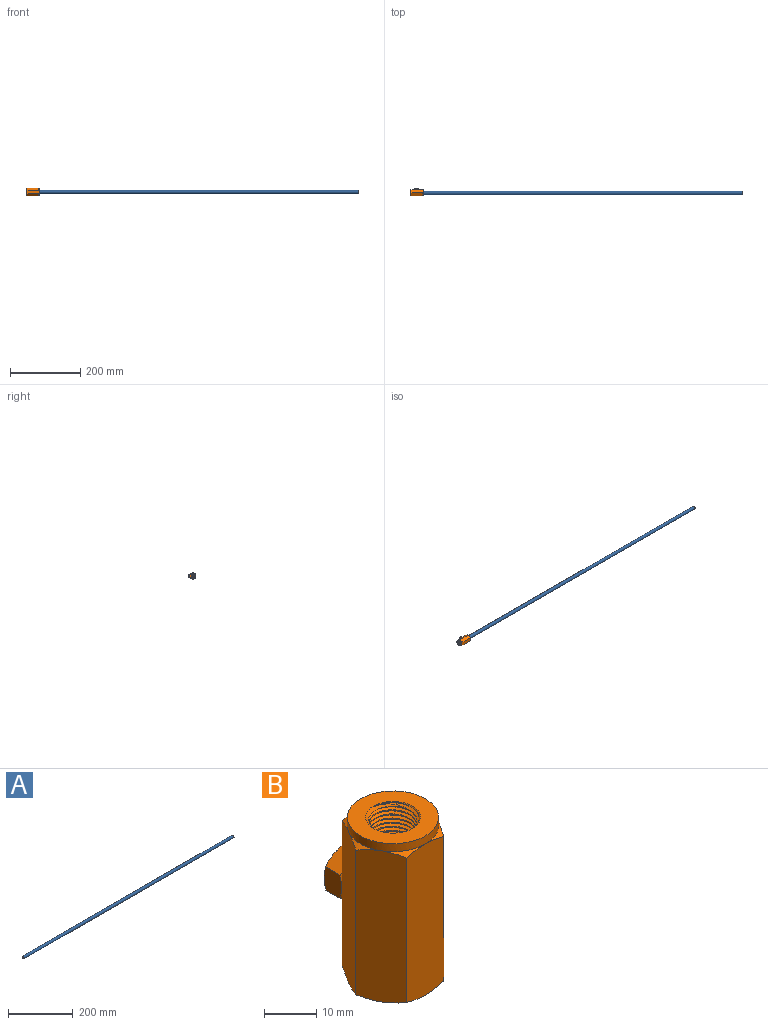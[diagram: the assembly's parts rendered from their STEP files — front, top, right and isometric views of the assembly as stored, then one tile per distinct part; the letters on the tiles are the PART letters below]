
ASSEMBLY  parts=2 mates=1
PART A: 4 faces, bbox 914.4x9.5x9.5 mm
  f0: cylinder r=3.52mm len=914.4mm, axis (-1,0,0), area 20211.5mm2, adj f2,f3
  f1: cylinder r=4.76mm len=914.4mm, axis (-1,0,0), area 27362.2mm2, adj f2,f3
  f2: plane 9.53x9.53mm, normal (1,0,0), area 32.4mm2, adj f0,f1
  f3: plane 9.53x9.53mm, normal (-1,0,0), area 32.4mm2, adj f0,f1
PART B: 55 faces, bbox 21x24.8x38.5 mm
  f0: cone r=5.5mm half-angle=60deg, axis (0,-1,0), area 2.2mm2, adj f43,f53,f54
  f1: cylinder r=4.76mm len=9.53mm, axis (0,-1,0), area 12.7mm2, adj f2,f12,f38,f39,f40,f41,f42
  f2: cone r=4.76mm half-angle=60deg, axis (0,1,0), area 2.2mm2, adj f1,f50,f51
  f3: cone r=5.25mm half-angle=45deg, axis (0,0,-1), area 18.3mm2, adj f8,f13,f35,f36,f37
  f4: cone r=5.25mm half-angle=45deg, axis (0,0,1), area 18.3mm2, adj f5,f6,f14,f32,f33,f34
  f5: cone r=5.25mm half-angle=45deg, axis (0,0,1), area 0mm2, adj f4,f33,f34
  f6: cone r=4.93mm half-angle=1.8deg, axis (0,0,1), area 23.2mm2, adj f4,f31,f32,f34
  f7: cylinder r=1.79mm len=23.9mm, axis (0,0,1), area 268.9mm2, adj f30,f31
  f8: cone r=5.14mm half-angle=1.8deg, axis (0,0,-1), area 23.2mm2, adj f3,f30,f35,f36
  f9: cylinder r=8.73mm len=17.46mm, axis (0,0,1), area 103.2mm2, adj f10,f14,f25,f26,f27,f28,f29
  f10: cone r=8.73mm half-angle=60deg, axis (0,0,-1), area 7.5mm2, adj f9,f15,f16
  f11: cone r=10.08mm half-angle=60deg, axis (0,0,1), area 7.5mm2, adj f13,f18,f19
  f12: plane 36.26x10.91mm, normal (0,1,0), area 280.5mm2, adj f1,f15,f19,f23,f24,f25,f29
  f13: plane 17.46x17.46mm, normal (0,0,-1), area 153.1mm2, adj f3,f11,f20,f21,f22,f23,f24
  f14: plane 17.46x17.46mm, normal (0,0,1), area 153.1mm2, adj f4,f9
  f15: plane 36.25x9.56mm, normal (-0.87,0.5,0), area 351.8mm2, adj f10,f12,f16,f22,f23,f25
  f16: plane 36.25x9.56mm, normal (-0.87,-0.5,0), area 351.8mm2, adj f10,f15,f17,f21,f22,f26
  f17: plane 36.26x10.91mm, normal (0,-1,0), area 351.8mm2, adj f16,f18,f20,f21,f26,f27
  f18: plane 36.25x9.56mm, normal (0.87,-0.5,0), area 351.8mm2, adj f11,f17,f19,f20,f27,f28
  f19: plane 36.25x9.56mm, normal (0.87,0.5,0), area 351.8mm2, adj f11,f12,f18,f24,f28,f29
  f20: cone r=10.08mm half-angle=60deg, axis (0,0,1), area 7.5mm2, adj f13,f17,f18
  f21: cone r=10.08mm half-angle=60deg, axis (0,0,1), area 7.5mm2, adj f13,f16,f17
  f22: cone r=10.08mm half-angle=60deg, axis (0,0,1), area 7.5mm2, adj f13,f15,f16
  f23: cone r=10.08mm half-angle=60deg, axis (0,0,1), area 7.5mm2, adj f12,f13,f15
  f24: cone r=10.08mm half-angle=60deg, axis (0,0,1), area 7.5mm2, adj f12,f13,f19
  f25: cone r=8.73mm half-angle=60deg, axis (0,0,-1), area 7.5mm2, adj f9,f12,f15
  f26: cone r=8.73mm half-angle=60deg, axis (0,0,-1), area 7.5mm2, adj f9,f16,f17
  f27: cone r=8.73mm half-angle=60deg, axis (0,0,-1), area 7.5mm2, adj f9,f17,f18
  f28: cone r=8.73mm half-angle=60deg, axis (0,0,-1), area 7.5mm2, adj f9,f18,f19
  f29: cone r=8.73mm half-angle=60deg, axis (0,0,-1), area 7.5mm2, adj f9,f12,f19
  f30: plane 9.61x9.54mm, normal (0,0,-1), area 57.6mm2, adj f7,f8,f35,f36,f37
  f31: plane 9.61x9.54mm, normal (0,0,1), area 57.6mm2, adj f6,f7,f32,f33,f34
  f32: bspline ~11.79x11.54mm, area 157.3mm2, adj f4,f6,f31,f33
  f33: bspline ~9.16x9.09mm, area 42.9mm2, adj f4,f5,f31,f32,f34
  f34: bspline ~10.49x10.45mm, area 124.8mm2, adj f4,f5,f6,f31,f33
  f35: bspline ~10.49x10.45mm, area 124.8mm2, adj f3,f8,f30,f37
  f36: bspline ~11.79x11.54mm, area 157.3mm2, adj f3,f8,f30,f37
  f37: bspline ~9.16x9.09mm, area 42.9mm2, adj f3,f30,f35,f36
  f38: cone r=4.76mm half-angle=60deg, axis (0,1,0), area 2.2mm2, adj f1,f51,f52
  f39: cone r=4.76mm half-angle=60deg, axis (0,1,0), area 2.2mm2, adj f1,f52,f53
  f40: cone r=4.76mm half-angle=60deg, axis (0,1,0), area 2.2mm2, adj f1,f53,f54
  f41: cone r=4.76mm half-angle=60deg, axis (0,1,0), area 2.2mm2, adj f1,f49,f54
  f42: cone r=4.76mm half-angle=60deg, axis (0,1,0), area 2.2mm2, adj f1,f49,f50
  f43: plane 9.53x9.53mm, normal (0,1,0), area 71.3mm2, adj f0,f44,f45,f46,f47,f48
  f44: cone r=5.5mm half-angle=60deg, axis (0,-1,0), area 2.2mm2, adj f43,f52,f53
  f45: cone r=5.5mm half-angle=60deg, axis (0,-1,0), area 2.2mm2, adj f43,f51,f52
  f46: cone r=5.5mm half-angle=60deg, axis (0,-1,0), area 2.2mm2, adj f43,f50,f51
  f47: cone r=5.5mm half-angle=60deg, axis (0,-1,0), area 2.2mm2, adj f43,f49,f50
  f48: cone r=5.5mm half-angle=60deg, axis (0,-1,0), area 2.2mm2, adj f43,f49,f54
  f49: plane 5.95x5.19mm, normal (1,0,0), area 24.4mm2, adj f41,f42,f47,f48,f50,f54
  f50: plane 5.21x5.19mm, normal (0.5,0,0.87), area 24.4mm2, adj f2,f42,f46,f47,f49,f51
  f51: plane 5.21x5.19mm, normal (-0.5,0,0.87), area 24.4mm2, adj f2,f38,f45,f46,f50,f52
  f52: plane 5.95x5.19mm, normal (-1,0,0), area 24.4mm2, adj f38,f39,f44,f45,f51,f53
  f53: plane 5.21x5.19mm, normal (-0.5,0,-0.87), area 24.4mm2, adj f0,f39,f40,f44,f52,f54
  f54: plane 5.21x5.19mm, normal (0.5,0,-0.87), area 24.4mm2, adj f0,f40,f41,f48,f49,f53
PLACE A rot(axis=(0,1,0),180deg) t=(469.15,0,0)mm
PLACE B rot(axis=(0,-1,0),90deg) t=(0,0,0)mm
MATE fastened A.f0 <-> B.f6  axis (1,0,0) through (11.95,0,0)mm
